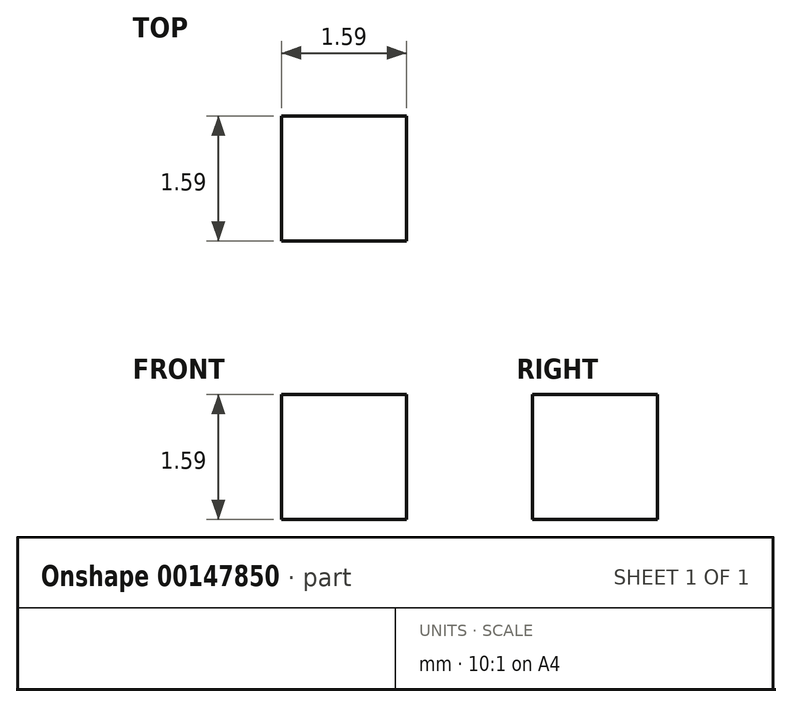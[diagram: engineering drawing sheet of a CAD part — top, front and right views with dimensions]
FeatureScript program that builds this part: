
annotation { "Feature Type Name" : "Feature", "Feature Type Description" : "" }
export const myFeature = defineFeature(function(context is Context, id is Id, definition is map)
    precondition{}
    {
        {
            var Q0;
            Q0=qCreatedBy(makeId("Top.planeOp"),FACE);
            var sketch = newSketch(context, id + "F0", { "sketchPlane" : qUnion([Q0])});
            skLineSegment(sketch, "E0.bottom", {"start": v(0, 0) * mm, "end": v(1.59, 0) * mm});
            skLineSegment(sketch, "E0.top", {"start": v(0, -1.59) * mm, "end": v(1.59, -1.59) * mm});
            skLineSegment(sketch, "E0.left", {"start": v(0, 0) * mm, "end": v(0, -1.59) * mm});
            skLineSegment(sketch, "E0.right", {"start": v(1.59, 0) * mm, "end": v(1.59, -1.59) * mm});
            skSolve(sketch);
        }
        {
            var Q0;
            Q0=qSketchRegion(id+"F0",true);
            extrude(context, id + "F1", {"entities" : qUnion([Q0]), "depth" : 1.59 * mm});
        }
    });
